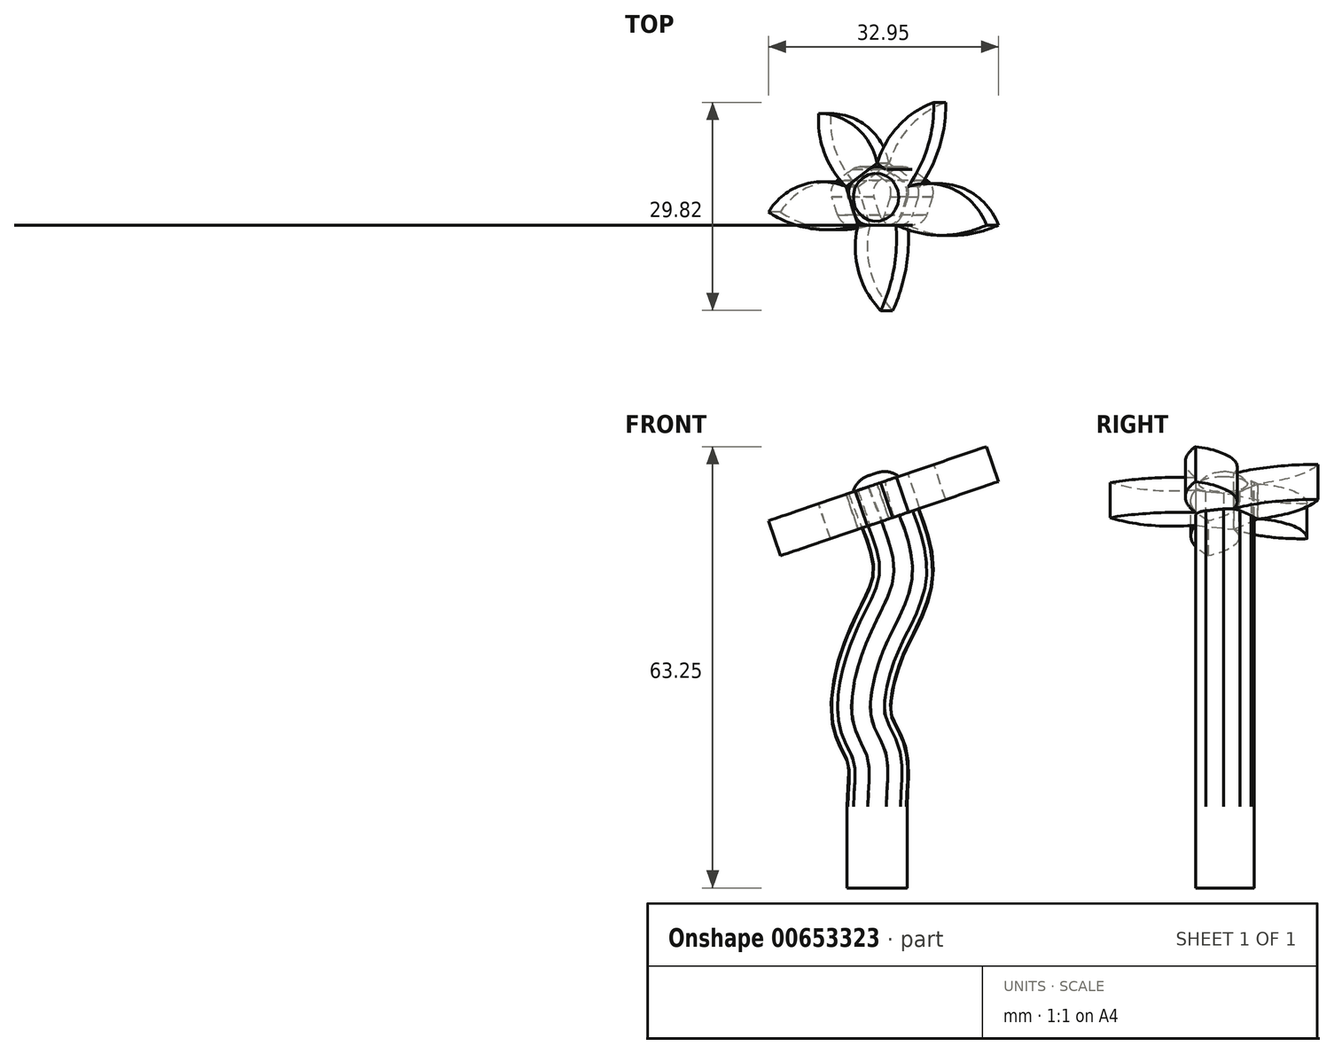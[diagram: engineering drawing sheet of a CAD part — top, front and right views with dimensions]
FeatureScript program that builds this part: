
annotation { "Feature Type Name" : "Feature", "Feature Type Description" : "" }
export const myFeature = defineFeature(function(context is Context, id is Id, definition is map)
    precondition{}
    {
        {
            var Q0;
            Q0=qCreatedBy(makeId("Top.planeOp"),FACE);
            var sketch = newSketch(context, id + "F0", { "sketchPlane" : qUnion([Q0])});
            skCircle(sketch, "E0.cCircle", {"center": v(0, 0) * mm, "radius": 3.97 * mm, "construction": true});
            skLineSegment(sketch, "E0.0", {"start": v(2.89, -3.97) * mm, "end": v(-2.89, -3.97) * mm});
            skLineSegment(sketch, "E0.1", {"start": v(-2.89, -3.97) * mm, "end": v(-4.67, 1.52) * mm});
            skLineSegment(sketch, "E0.2", {"start": v(-4.67, 1.52) * mm, "end": v(0, 4.91) * mm});
            skLineSegment(sketch, "E0.3", {"start": v(0, 4.91) * mm, "end": v(4.67, 1.52) * mm});
            skLineSegment(sketch, "E0.4", {"start": v(4.67, 1.52) * mm, "end": v(2.89, -3.97) * mm});
            skPoint(sketch, "E0.0.midPoint", {"position": v(0, -3.97) * mm});
            skSolve(sketch);
        }
        {
            var Q0;
            Q0=qCreatedBy(makeId("Front.planeOp"),FACE);
            var sketch = newSketch(context, id + "F1", { "sketchPlane" : qUnion([Q0])});
            skLineSegment(sketch, "E1", {"start": v(0, 0) * mm, "end": v(0, 11.64) * mm});
            skFitSpline(sketch, "E2", {"points": [v(0, 11.64) * mm, v(0, 18.8) * mm, v(-2.13, 24.03) * mm, v(0, 35.35) * mm, v(3.76, 45.56) * mm, v(0, 57.91) * mm], "startDerivative": vector(0, 37.52) * mm, "endDerivative": vector(-16.77, 49.3) * mm});
            skSolve(sketch);
        }
        {
            var Q0;
            Q0=makeQuery(id+"F0.imprint","IMPRINT",FACE,{"disambiguationData":[TD([[makeQuery(id+"F0.imprint","IMPRINT",EDGE,{"derivedFrom":sQuery(id+"F0.wireOp",EDGE,"E0.0")}),-1.0]])]});
            var Q1;
            Q1=sQuery(id+"F1.wireOp",EDGE,"E1");
            var Q2;
            Q2=sQuery(id+"F1.wireOp",EDGE,"E2");
            sweep(context, id + "F2", {"profiles" : qUnion([Q0]), "path" : qUnion([Q1, Q2])});
        }
        {
            var Q0;
            Q0=makeQuery(id+"F2.opSweep","CAP_FACE",FACE,{"disambiguationData":[OSD([sQuery(id+"F0.wireOp",EDGE,"E0.0"),sQuery(id+"F0.wireOp",EDGE,"E0.1"),sQuery(id+"F0.wireOp",EDGE,"E0.2"),sQuery(id+"F0.wireOp",EDGE,"E0.3"),sQuery(id+"F0.wireOp",EDGE,"E0.4"),sQuery(id+"F1.wireOp",VERTEX,"E2.end")])],"isStart":false});
            var sketch = newSketch(context, id + "F3", { "sketchPlane" : qUnion([Q0])});
            skCircle(sketch, "E3", {"center": v(18.49, 0) * mm, "radius": 3.45 * mm});
            skSolve(sketch);
        }
        {
            var Q0;
            Q0 = qSketchRegion(id + "F3", true);
            extrude(context, id + "F4", {"entities" : qUnion([Q0]), "operationType" : NewBodyOperationType.ADD, "depth" : 1.5 * mm, "offsetDistance" : 25 * mm});
        }
        {
            var Q0;
            Q0=makeQuery(id+"F4.opExtrude","CAP_FACE",FACE,{"disambiguationData":[OSD([sQuery(id+"F3.wireOp",EDGE,"E3")])],"isStart":false});
            fillet(context, id + "F5", {"entities" : qUnion([Q0]), "radius" : 3.38 * mm, "tangentPropagation" : true, "allowEdgeOverflow" : false});
        }
        {
            var Q0;
            Q0=makeQuery(id+"F2.opSweep","CAP_FACE",FACE,{"disambiguationData":[OSD([sQuery(id+"F0.wireOp",EDGE,"E0.0"),sQuery(id+"F0.wireOp",EDGE,"E0.1"),sQuery(id+"F0.wireOp",EDGE,"E0.2"),sQuery(id+"F0.wireOp",EDGE,"E0.3"),sQuery(id+"F0.wireOp",EDGE,"E0.4"),sQuery(id+"F1.wireOp",VERTEX,"E2.end")])],"isStart":false});
            var sketch = newSketch(context, id + "F6", { "sketchPlane" : qUnion([Q0])});
            skArc(sketch, "E4", {"start": v(27.24, 13.6) * mm, "mid": v(21.93, 10.26) * mm, "end": v(18.65, 4.91) * mm});
            skArc(sketch, "E5", {"start": v(23.32, 1.52) * mm, "mid": v(26.3, 7.23) * mm, "end": v(27.24, 13.6) * mm});
            skArc(sketch, "E6", {"start": v(19.23, -16.22) * mm, "mid": v(21.2, -10.25) * mm, "end": v(21.54, -3.97) * mm});
            skArc(sketch, "E7", {"start": v(15.76, -3.97) * mm, "mid": v(15.83, -10.57) * mm, "end": v(19.23, -16.22) * mm});
            skArc(sketch, "E8", {"start": v(2.22, -2.1) * mm, "mid": v(8.79, -4.5) * mm, "end": v(15.76, -3.97) * mm});
            skArc(sketch, "E9", {"start": v(13.98, 1.52) * mm, "mid": v(7.45, 1.81) * mm, "end": v(2.22, -2.1) * mm});
            skArc(sketch, "E10", {"start": v(9.8, 11.99) * mm, "mid": v(10.7, 6.28) * mm, "end": v(13.98, 1.52) * mm});
            skArc(sketch, "E11", {"start": v(18.65, 4.91) * mm, "mid": v(15.5, 10.03) * mm, "end": v(9.8, 11.99) * mm});
            skArc(sketch, "E12", {"start": v(21.54, -3.97) * mm, "mid": v(28.38, -5.44) * mm, "end": v(35.22, -3.97) * mm});
            skArc(sketch, "E13", {"start": v(35.22, -3.97) * mm, "mid": v(30.34, 1.1) * mm, "end": v(23.32, 1.52) * mm});
            skSolve(sketch);
        }
        {
            var Q0;
            Q0=makeQuery(id+"F6.imprint","IMPRINT",FACE,{"disambiguationData":[TD([[makeQuery(id+"F6.imprint","IMPRINT",EDGE,{"derivedFrom":sQuery(id+"F6.wireOp",EDGE,"E12")}),1.0]])]});
            var Q1;
            Q1=makeQuery(id+"F6.imprint","IMPRINT",FACE,{"disambiguationData":[TD([[makeQuery(id+"F6.imprint","IMPRINT",EDGE,{"derivedFrom":sQuery(id+"F6.wireOp",EDGE,"E4")}),1.0]])]});
            var Q2;
            Q2=makeQuery(id+"F6.imprint","IMPRINT",FACE,{"disambiguationData":[TD([[makeQuery(id+"F6.imprint","IMPRINT",EDGE,{"derivedFrom":sQuery(id+"F6.wireOp",EDGE,"E10")}),1.0]])]});
            var Q3;
            Q3=makeQuery(id+"F6.imprint","IMPRINT",FACE,{"disambiguationData":[TD([[makeQuery(id+"F6.imprint","IMPRINT",EDGE,{"derivedFrom":sQuery(id+"F6.wireOp",EDGE,"E8")}),1.0]])]});
            var Q4;
            Q4=makeQuery(id+"F6.imprint","IMPRINT",FACE,{"disambiguationData":[TD([[makeQuery(id+"F6.imprint","IMPRINT",EDGE,{"derivedFrom":sQuery(id+"F6.wireOp",EDGE,"E6")}),1.0]])]});
            extrude(context, id + "F7", {"entities" : qUnion([Q0, Q1, Q2, Q3, Q4]), "operationType" : NewBodyOperationType.ADD, "oppositeDirection" : true, "depth" : 5.3 * mm, "offsetDistance" : 25 * mm});
        }
        {
            var Q0;
            Q0=makeQuery(id+"F2.opSweep","SWEPT_EDGE",EDGE,{"disambiguationData":[OSD([sQuery(id+"F0.wireOp",EDGE,"E0.1"),sQuery(id+"F0.wireOp",EDGE,"E0.2"),sQuery(id+"F1.wireOp",EDGE,"E2")])]});
            var Q1;
            Q1=makeQuery(id+"F2.opSweep","SWEPT_EDGE",EDGE,{"disambiguationData":[OSD([sQuery(id+"F0.wireOp",EDGE,"E0.1"),sQuery(id+"F0.wireOp",EDGE,"E0.2"),sQuery(id+"F1.wireOp",EDGE,"E1")])]});
            var Q2;
            Q2=makeQuery(id+"F2.opSweep","SWEPT_EDGE",EDGE,{"disambiguationData":[OSD([sQuery(id+"F0.wireOp",EDGE,"E0.2"),sQuery(id+"F0.wireOp",EDGE,"E0.3"),sQuery(id+"F1.wireOp",EDGE,"E1")])]});
            var Q3;
            Q3=makeQuery(id+"F2.opSweep","SWEPT_EDGE",EDGE,{"disambiguationData":[OSD([sQuery(id+"F0.wireOp",EDGE,"E0.2"),sQuery(id+"F0.wireOp",EDGE,"E0.3"),sQuery(id+"F1.wireOp",EDGE,"E2")])]});
            var Q4;
            {var subQ0=sQuery(id+"F0.wireOp",EDGE,"E0.0");var subQ1=sQuery(id+"F1.wireOp",EDGE,"E2");var subQ2=sQuery(id+"F0.wireOp",EDGE,"E0.1");Q4=makeQuery(id+"F7.boolean.opBoolean","SPLIT",EDGE,{"disambiguationData":[topologyDisambiguationEdgeConnected([makeQuery(id+"F2.opSweep","SWEPT_FACE",FACE,{"disambiguationData":[OSD([subQ0,sQuery(id+"F1.wireOp",EDGE,"E1")])]})])],"derivedFrom":makeQuery(id+"F2.opSweep","SWEPT_EDGE",EDGE,{"disambiguationData":[OSD([subQ0,subQ2,subQ1])]})});}
            var Q5;
            Q5=makeQuery(id+"F2.opSweep","SWEPT_EDGE",EDGE,{"disambiguationData":[OSD([sQuery(id+"F0.wireOp",EDGE,"E0.0"),sQuery(id+"F0.wireOp",EDGE,"E0.1"),sQuery(id+"F1.wireOp",EDGE,"E1")])]});
            var Q6;
            Q6=makeQuery(id+"F2.opSweep","SWEPT_EDGE",EDGE,{"disambiguationData":[OSD([sQuery(id+"F0.wireOp",EDGE,"E0.0"),sQuery(id+"F0.wireOp",EDGE,"E0.4"),sQuery(id+"F1.wireOp",EDGE,"E2")])]});
            var Q7;
            Q7=makeQuery(id+"F2.opSweep","SWEPT_EDGE",EDGE,{"disambiguationData":[OSD([sQuery(id+"F0.wireOp",EDGE,"E0.0"),sQuery(id+"F0.wireOp",EDGE,"E0.4"),sQuery(id+"F1.wireOp",EDGE,"E1")])]});
            var Q8;
            Q8=makeQuery(id+"F2.opSweep","SWEPT_EDGE",EDGE,{"disambiguationData":[OSD([sQuery(id+"F0.wireOp",EDGE,"E0.3"),sQuery(id+"F0.wireOp",EDGE,"E0.4"),sQuery(id+"F1.wireOp",EDGE,"E2")])]});
            var Q9;
            Q9=makeQuery(id+"F2.opSweep","SWEPT_EDGE",EDGE,{"disambiguationData":[OSD([sQuery(id+"F0.wireOp",EDGE,"E0.3"),sQuery(id+"F0.wireOp",EDGE,"E0.4"),sQuery(id+"F1.wireOp",EDGE,"E1")])]});
            fillet(context, id + "F8", {"entities" : qUnion([Q0, Q1, Q2, Q3, Q4, Q5, Q6, Q7, Q8, Q9]), "radius" : 2.12 * mm, "tangentPropagation" : true, "allowEdgeOverflow" : false});
        }
    });
